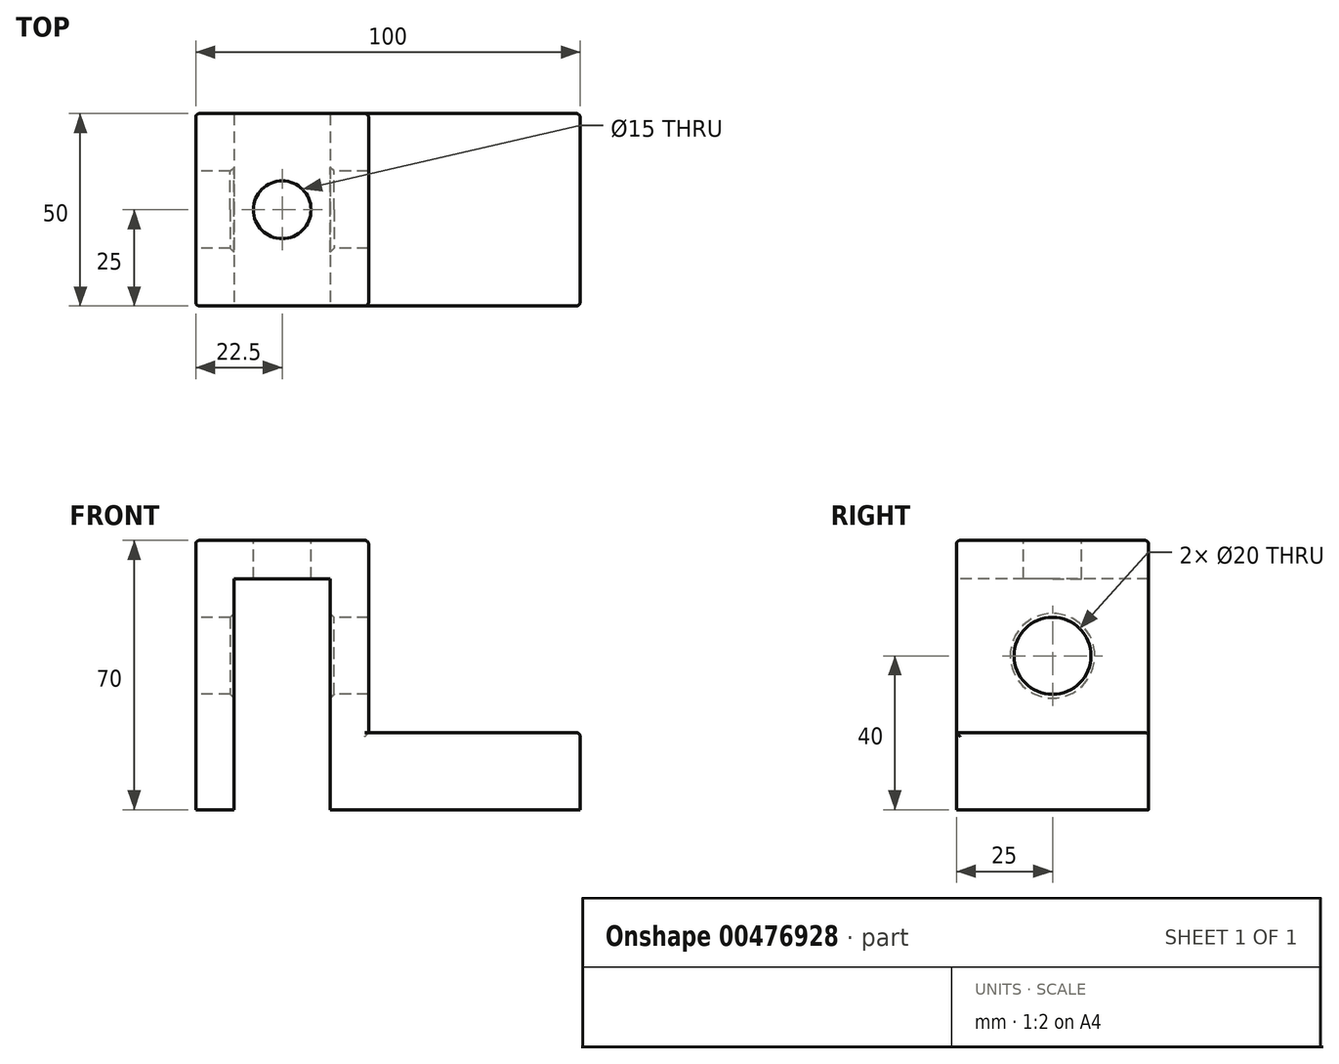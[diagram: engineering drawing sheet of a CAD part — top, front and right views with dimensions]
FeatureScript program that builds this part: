
annotation { "Feature Type Name" : "Feature", "Feature Type Description" : "" }
export const myFeature = defineFeature(function(context is Context, id is Id, definition is map)
    precondition{}
    {
        {
            var Q0;
            Q0=qCreatedBy(makeId("Top.planeOp"),FACE);
            var sketch = newSketch(context, id + "F0", { "sketchPlane" : qUnion([Q0])});
            skLineSegment(sketch, "E0.bottom", {"start": v(0, 0) * mm, "end": v(100, 0) * mm});
            skLineSegment(sketch, "E0.top", {"start": v(0, 50) * mm, "end": v(100, 50) * mm});
            skLineSegment(sketch, "E0.left", {"start": v(0, 0) * mm, "end": v(0, 50) * mm});
            skLineSegment(sketch, "E0.right", {"start": v(100, 0) * mm, "end": v(100, 50) * mm});
            skSolve(sketch);
        }
        {
            var Q0;
            Q0 = qSketchRegion(id + "F0", true);
            extrude(context, id + "F1", {"entities" : qUnion([Q0]), "depth" : 20 * mm});
        }
        {
            var Q0;
            Q0=makeQuery(id+"F1.opExtrude","CAP_FACE",FACE,{"disambiguationData":[OSD([sQuery(id+"F0.wireOp",EDGE,"E0.bottom"),sQuery(id+"F0.wireOp",EDGE,"E0.top"),sQuery(id+"F0.wireOp",EDGE,"E0.left"),sQuery(id+"F0.wireOp",EDGE,"E0.right")])],"isStart":false});
            var sketch = newSketch(context, id + "F2", { "sketchPlane" : qUnion([Q0])});
            skLineSegment(sketch, "E1.bottom", {"start": v(0, 0) * mm, "end": v(45, 0) * mm});
            skLineSegment(sketch, "E1.top", {"start": v(0, 50) * mm, "end": v(45, 50) * mm});
            skLineSegment(sketch, "E1.left", {"start": v(0, 0) * mm, "end": v(0, 50) * mm});
            skLineSegment(sketch, "E1.right", {"start": v(45, 0) * mm, "end": v(45, 50) * mm});
            skSolve(sketch);
        }
        {
            var Q0;
            Q0 = qSketchRegion(id + "F2", true);
            extrude(context, id + "F3", {"entities" : qUnion([Q0]), "operationType" : NewBodyOperationType.ADD, "depth" : 50 * mm});
        }
        {
            var Q0;
            Q0=makeQuery(id+"F3.boolean.opBoolean","MERGE",FACE,{"derivedFrom":[makeQuery(id+"F1.opExtrude","SWEPT_FACE",FACE,{"disambiguationData":[OSD([sQuery(id+"F0.wireOp",EDGE,"E0.bottom")])]}),makeQuery(id+"F3.opExtrude","SWEPT_FACE",FACE,{"disambiguationData":[OSD([sQuery(id+"F2.wireOp",EDGE,"E1.bottom")])]})]});
            var sketch = newSketch(context, id + "F4", { "sketchPlane" : qUnion([Q0])});
            skLineSegment(sketch, "E2.bottom", {"start": v(10, 0) * mm, "end": v(35, 0) * mm});
            skLineSegment(sketch, "E2.top", {"start": v(10, 60) * mm, "end": v(35, 60) * mm});
            skLineSegment(sketch, "E2.left", {"start": v(10, 0) * mm, "end": v(10, 60) * mm});
            skLineSegment(sketch, "E2.right", {"start": v(35, 0) * mm, "end": v(35, 60) * mm});
            skSolve(sketch);
        }
        {
            var Q0;
            Q0 = qSketchRegion(id + "F4", true);
            extrude(context, id + "F5", {"entities" : qUnion([Q0]), "operationType" : NewBodyOperationType.REMOVE, "endBound" : BoundingType.THROUGH_ALL, "oppositeDirection" : true, "depth" : 25 * mm});
        }
        {
            var Q0;
            Q0=makeQuery(id+"F3.boolean.opBoolean","MERGE",FACE,{"derivedFrom":[makeQuery(id+"F1.opExtrude","SWEPT_FACE",FACE,{"disambiguationData":[OSD([sQuery(id+"F0.wireOp",EDGE,"E0.left")])]}),makeQuery(id+"F3.opExtrude","SWEPT_FACE",FACE,{"disambiguationData":[OSD([sQuery(id+"F2.wireOp",EDGE,"E1.left")])]})]});
            var sketch = newSketch(context, id + "F6", { "sketchPlane" : qUnion([Q0])});
            skCircle(sketch, "E3", {"center": v(-25, 40) * mm, "radius": 10 * mm});
            skSolve(sketch);
        }
        {
            var Q0;
            Q0 = qSketchRegion(id + "F6", true);
            var Q1;
            Q1=makeQuery(id+"F3.opExtrude","SWEPT_FACE",FACE,{"disambiguationData":[OSD([sQuery(id+"F2.wireOp",EDGE,"E1.right")])]});
            extrude(context, id + "F7", {"entities" : qUnion([Q0]), "operationType" : NewBodyOperationType.REMOVE, "endBound" : BoundingType.UP_TO_SURFACE, "oppositeDirection" : true, "endBoundEntityFace" : qUnion([Q1]), "depth" : 25 * mm});
        }
        {
            var Q0;
            Q0=makeQuery(id+"F3.opExtrude","CAP_FACE",FACE,{"disambiguationData":[OSD([sQuery(id+"F2.wireOp",EDGE,"E1.bottom"),sQuery(id+"F2.wireOp",EDGE,"E1.top"),sQuery(id+"F2.wireOp",EDGE,"E1.left"),sQuery(id+"F2.wireOp",EDGE,"E1.right")])],"isStart":false});
            var sketch = newSketch(context, id + "F8", { "sketchPlane" : qUnion([Q0])});
            skLineSegment(sketch, "E4", {"start": v(45, 0) * mm, "end": v(0, 50) * mm, "construction": true});
            skLineSegment(sketch, "E5", {"start": v(45, 50) * mm, "end": v(0, 0) * mm, "construction": true});
            skCircle(sketch, "E6", {"center": v(22.5, 25) * mm, "radius": 7.5 * mm});
            skSolve(sketch);
        }
        {
            var Q0;
            Q0 = qSketchRegion(id + "F8", true);
            extrude(context, id + "F9", {"entities" : qUnion([Q0]), "operationType" : NewBodyOperationType.REMOVE, "endBound" : BoundingType.UP_TO_NEXT, "oppositeDirection" : true, "depth" : 25 * mm});
        }
        {
            var Q0;
            Q0=makeQuery(id+"F3.opExtrude","CAP_EDGE",EDGE,{"disambiguationData":[OSD([sQuery(id+"F2.wireOp",EDGE,"E1.right")])],"isStart":false});
            var Q1;
            Q1=makeQuery(id+"F3.opExtrude","CAP_EDGE",EDGE,{"disambiguationData":[OSD([sQuery(id+"F2.wireOp",EDGE,"E1.right")])],"isStart":true});
            var Q2;
            Q2=makeQuery(id+"F3.opExtrude","SWEPT_EDGE",EDGE,{"disambiguationData":[OSD([sQuery(id+"F0.wireOp",EDGE,"E0.bottom"),sQuery(id+"F2.wireOp",EDGE,"E1.bottom"),sQuery(id+"F2.wireOp",EDGE,"E1.right")])]});
            var Q3;
            Q3=makeQuery(id+"F3.opExtrude","CAP_EDGE",EDGE,{"disambiguationData":[OSD([sQuery(id+"F2.wireOp",EDGE,"E1.bottom")])],"isStart":false});
            var Q4;
            Q4=makeQuery(id+"F3.boolean.opBoolean","MERGE",EDGE,{"derivedFrom":[makeQuery(id+"F1.opExtrude","SWEPT_EDGE",EDGE,{"disambiguationData":[OSD([sQuery(id+"F0.wireOp",EDGE,"E0.bottom"),sQuery(id+"F0.wireOp",EDGE,"E0.left")])]}),makeQuery(id+"F3.opExtrude","SWEPT_EDGE",EDGE,{"disambiguationData":[OSD([sQuery(id+"F2.wireOp",EDGE,"E1.bottom"),sQuery(id+"F2.wireOp",EDGE,"E1.left")])]})]});
            var Q5;
            Q5=makeQuery(id+"F3.opExtrude","CAP_EDGE",EDGE,{"disambiguationData":[OSD([sQuery(id+"F2.wireOp",EDGE,"E1.left")])],"isStart":false});
            var Q6;
            Q6=makeQuery(id+"F3.opExtrude","CAP_EDGE",EDGE,{"disambiguationData":[OSD([sQuery(id+"F2.wireOp",EDGE,"E1.top")])],"isStart":false});
            var Q7;
            Q7=makeQuery(id+"F3.opExtrude","SWEPT_EDGE",EDGE,{"disambiguationData":[OSD([sQuery(id+"F0.wireOp",EDGE,"E0.top"),sQuery(id+"F2.wireOp",EDGE,"E1.top"),sQuery(id+"F2.wireOp",EDGE,"E1.right")])]});
            var Q8;
            Q8=makeQuery(id+"F1.opExtrude","CAP_EDGE",EDGE,{"disambiguationData":[OSD([sQuery(id+"F0.wireOp",EDGE,"E0.top")])],"isStart":false});
            var Q9;
            Q9=makeQuery(id+"F1.opExtrude","CAP_EDGE",EDGE,{"disambiguationData":[OSD([sQuery(id+"F0.wireOp",EDGE,"E0.right")])],"isStart":false});
            var Q10;
            Q10=makeQuery(id+"F3.boolean.opBoolean","MERGE",EDGE,{"derivedFrom":[makeQuery(id+"F1.opExtrude","SWEPT_EDGE",EDGE,{"disambiguationData":[OSD([sQuery(id+"F0.wireOp",EDGE,"E0.top"),sQuery(id+"F0.wireOp",EDGE,"E0.left")])]}),makeQuery(id+"F3.opExtrude","SWEPT_EDGE",EDGE,{"disambiguationData":[OSD([sQuery(id+"F2.wireOp",EDGE,"E1.top"),sQuery(id+"F2.wireOp",EDGE,"E1.left")])]})]});
            var Q11;
            Q11=makeQuery(id+"F1.opExtrude","SWEPT_EDGE",EDGE,{"disambiguationData":[OSD([sQuery(id+"F0.wireOp",EDGE,"E0.bottom"),sQuery(id+"F0.wireOp",EDGE,"E0.right")])]});
            var Q12;
            Q12=makeQuery(id+"F1.opExtrude","SWEPT_EDGE",EDGE,{"disambiguationData":[OSD([sQuery(id+"F0.wireOp",EDGE,"E0.top"),sQuery(id+"F0.wireOp",EDGE,"E0.right")])]});
            fillet(context, id + "F10", {"entities" : qUnion([Q0, Q1, Q2, Q3, Q4, Q5, Q6, Q7, Q8, Q9, Q10, Q11, Q12]), "radius" : 1 * mm, "tangentPropagation" : true, "allowEdgeOverflow" : false});
        }
        {
            var Q0;
            Q0=makeQuery(id+"F7.boolean.opBoolean","COPY",EDGE,{"derivedFrom":makeQuery(id+"F7.opExtrude","CAP_EDGE",EDGE,{"disambiguationData":[OSD([sQuery(id+"F6.wireOp",EDGE,"E3")])],"isStart":false})});
            var Q1;
            Q1=makeQuery(id+"F7.boolean.opBoolean","INTERSECT",EDGE,{"derivedFrom":[makeQuery(id+"F5.boolean.opBoolean","COPY",FACE,{"derivedFrom":makeQuery(id+"F5.opExtrude","SWEPT_FACE",FACE,{"disambiguationData":[OSD([sQuery(id+"F4.wireOp",EDGE,"E2.left")])]})}),makeQuery(id+"F7.opExtrude","SWEPT_FACE",FACE,{"disambiguationData":[OSD([sQuery(id+"F6.wireOp",EDGE,"E3")])]})]});
            var Q2;
            Q2=makeQuery(id+"F7.boolean.opBoolean","INTERSECT",EDGE,{"derivedFrom":[makeQuery(id+"F5.boolean.opBoolean","COPY",FACE,{"derivedFrom":makeQuery(id+"F5.opExtrude","SWEPT_FACE",FACE,{"disambiguationData":[OSD([sQuery(id+"F4.wireOp",EDGE,"E2.right")])]})}),makeQuery(id+"F7.opExtrude","SWEPT_FACE",FACE,{"disambiguationData":[OSD([sQuery(id+"F6.wireOp",EDGE,"E3")])]})]});
            var Q3;
            Q3=makeQuery(id+"F7.boolean.opBoolean","COPY",EDGE,{"derivedFrom":makeQuery(id+"F7.opExtrude","CAP_EDGE",EDGE,{"disambiguationData":[OSD([sQuery(id+"F6.wireOp",EDGE,"E3")])],"isStart":true})});
            var Q4;
            Q4=makeQuery(id+"F9.boolean.opBoolean","COPY",EDGE,{"derivedFrom":makeQuery(id+"F9.opExtrude","CAP_EDGE",EDGE,{"disambiguationData":[OSD([sQuery(id+"F8.wireOp",EDGE,"E6")])],"isStart":true})});
            var Q5;
            Q5=makeQuery(id+"F9.boolean.opBoolean","COPY",EDGE,{"derivedFrom":makeQuery(id+"F9.opExtrude","CAP_EDGE",EDGE,{"disambiguationData":[OSD([sQuery(id+"F8.wireOp",EDGE,"E6")])],"isStart":false})});
            chamfer(context, id + "F11", {"entities" : qUnion([Q0, Q1, Q2, Q3, Q4, Q5]), "width" : 1 * mm, "tangentPropagation" : true});
        }
    });
